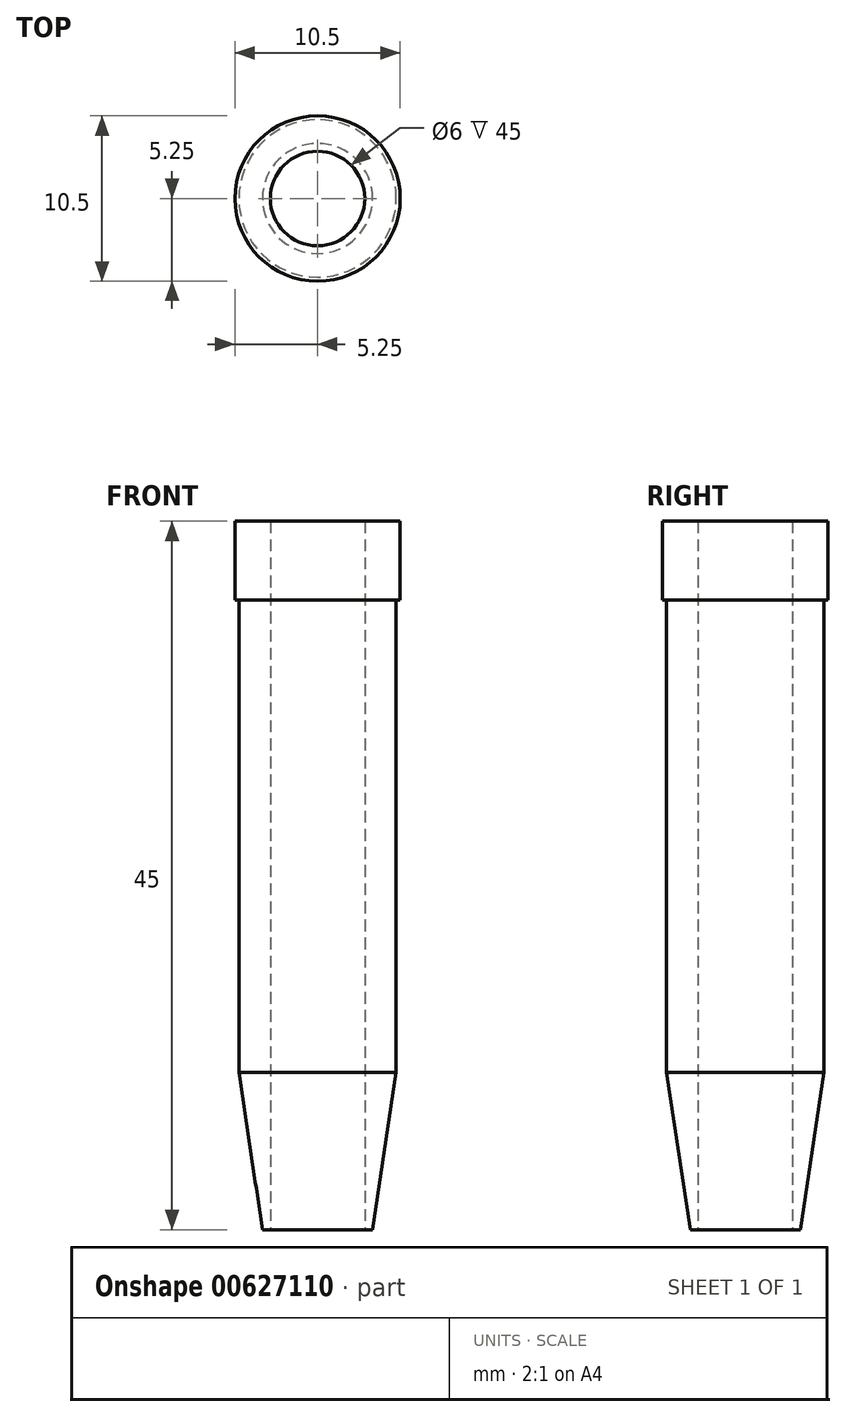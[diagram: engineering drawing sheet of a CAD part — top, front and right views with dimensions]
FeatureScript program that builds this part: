
annotation { "Feature Type Name" : "Feature", "Feature Type Description" : "" }
export const myFeature = defineFeature(function(context is Context, id is Id, definition is map)
    precondition{}
    {
        {
            var Q0;
            Q0=qCreatedBy(makeId("Front.planeOp"),FACE);
            var sketch = newSketch(context, id + "F0", { "sketchPlane" : qUnion([Q0])});
            skLineSegment(sketch, "E0", {"start": v(0, 0) * mm, "end": v(0, 51.85) * mm, "construction": true});
            skLineSegment(sketch, "E1", {"start": v(3, 45) * mm, "end": v(3, 0) * mm});
            skLineSegment(sketch, "E2", {"start": v(3, 0) * mm, "end": v(3.5, 0) * mm});
            skLineSegment(sketch, "E3", {"start": v(3.5, 0) * mm, "end": v(5, 10) * mm});
            skLineSegment(sketch, "E4", {"start": v(5, 10) * mm, "end": v(5, 40) * mm});
            skLineSegment(sketch, "E5", {"start": v(5.25, 40) * mm, "end": v(5, 40) * mm});
            skLineSegment(sketch, "E6", {"start": v(5.25, 40) * mm, "end": v(5.25, 45) * mm});
            skLineSegment(sketch, "E7", {"start": v(5.25, 45) * mm, "end": v(3, 45) * mm});
            skSolve(sketch);
        }
        {
            var Q0;
            Q0 = qSketchRegion(id + "F0", true);
            var Q1;
            Q1=sQuery(id+"F0.wireOp",EDGE,"E0");
            revolve(context, id + "F1", {"entities" : qUnion([Q0]), "axis" : qUnion([Q1]), "revolveType" : RevolveType.FULL});
        }
    });
